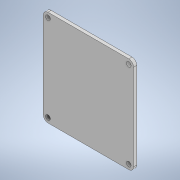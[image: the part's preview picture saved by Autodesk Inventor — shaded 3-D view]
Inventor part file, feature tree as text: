
AUTODESK INVENTOR PART (.ipt)
format: ipt  version: 2020 (Build 240168000, 168)  size: 120,832 bytes
history: native  units: mm
features: other x3, extrude x2, sketch x2, plane x1, reference x1
ambient origin geometry x8: Origin, YZ Plane, XZ Plane, XY Plane, X Axis, Y Axis, Z Axis, Center Point
bodies: 实体1 (feature_tree)
feature tree (9):
  plane  "工作平面1"
  extrude  "拉伸1"  Depth=4.0mm
  extrude  "拉伸2"  Depth=4.0mm
  sketch  "草图1"  dims[d0=4.0mm d1=0.0mm d2=0.5mm]
  reference  "参考1"
  sketch  "草图2"  dims[d3=0.5mm d4=0.5mm d5=0.5mm d6=4.0mm d7=0.0mm]
  other  "<userpath>\Desktop\ME_course_project\课设试试\shaft_try_1.iam"
  other  "shaft_try_1.iam"
  other  "shang(1):1"
